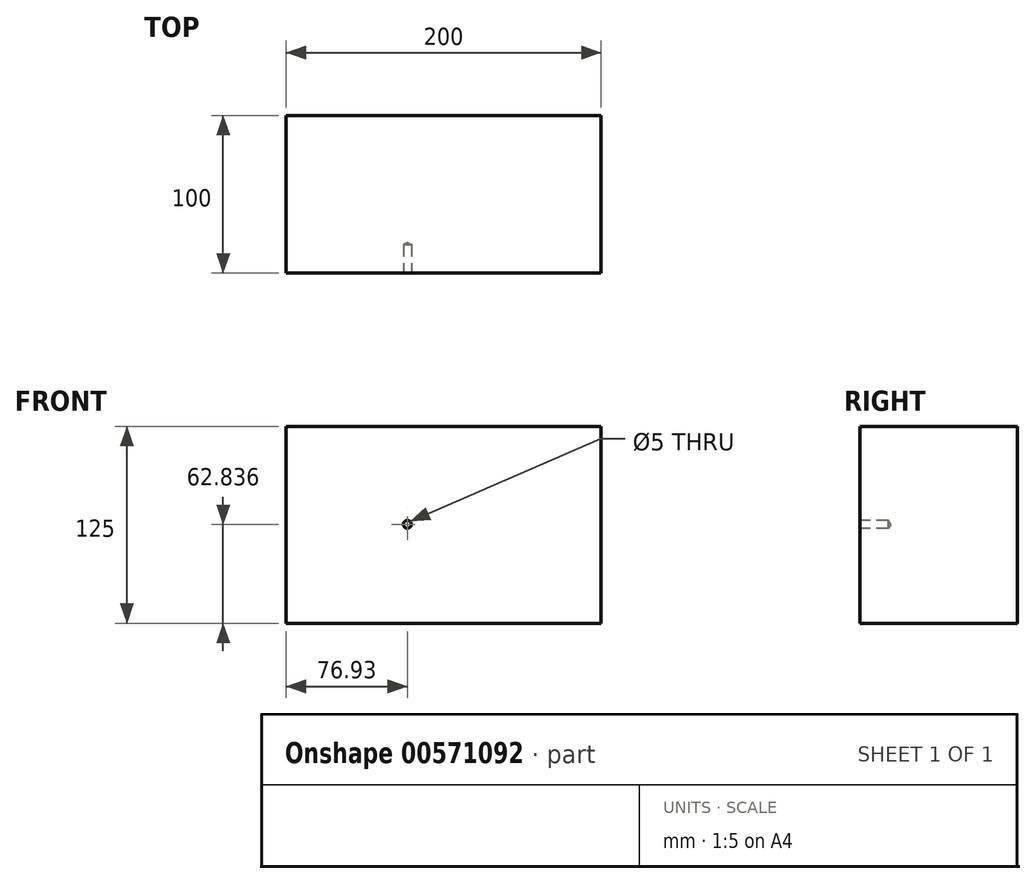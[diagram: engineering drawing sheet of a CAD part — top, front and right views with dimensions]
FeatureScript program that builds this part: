
annotation { "Feature Type Name" : "Feature", "Feature Type Description" : "" }
export const myFeature = defineFeature(function(context is Context, id is Id, definition is map)
    precondition{}
    {
        {
            var Q0;
            Q0=qCreatedBy(makeId("Front.planeOp"),FACE);
            var sketch = newSketch(context, id + "F0", { "sketchPlane" : qUnion([Q0])});
            skLineSegment(sketch, "E0.bottom", {"start": v(-100, 50) * mm, "end": v(100, 50) * mm});
            skLineSegment(sketch, "E0.top", {"start": v(-100, -50) * mm, "end": v(100, -50) * mm});
            skLineSegment(sketch, "E0.left", {"start": v(-100, 50) * mm, "end": v(-100, -50) * mm});
            skLineSegment(sketch, "E0.right", {"start": v(100, 50) * mm, "end": v(100, -50) * mm});
            skPoint(sketch, "E0.middle", {"position": v(0, 0) * mm});
            skSolve(sketch);
        }
        {
            var Q0;
            Q0 = qSketchRegion(id + "F0", true);
            extrude(context, id + "F1", {"entities" : qUnion([Q0]), "endBound" : BoundingType.SYMMETRIC, "depth" : 100 * mm, "offsetDistance" : 25 * mm});
        }
        {
            var Q0;
            Q0=makeQuery(id+"F1.opExtrude","CAP_FACE",FACE,{"disambiguationData":[OSD([sQuery(id+"F0.wireOp",EDGE,"E0.bottom"),sQuery(id+"F0.wireOp",EDGE,"E0.top"),sQuery(id+"F0.wireOp",EDGE,"E0.left"),sQuery(id+"F0.wireOp",EDGE,"E0.right")])],"isStart":false});
            var sketch = newSketch(context, id + "F2", { "sketchPlane" : qUnion([Q0])});
            skPoint(sketch, "E1", {"position": v(-23.07, 12.84) * mm});
            skSolve(sketch);
        }
        {
            var Q0;
            Q0=sQuery(id+"F2.wireOp",VERTEX,"E1");
            var Q1;
            Q1=makeQuery(id+"F1.opExtrude","SWEPT_BODY",BODY,{"disambiguationData":[OSD([sQuery(id+"F0.wireOp",EDGE,"E0.bottom"),sQuery(id+"F0.wireOp",EDGE,"E0.top"),sQuery(id+"F0.wireOp",EDGE,"E0.left"),sQuery(id+"F0.wireOp",EDGE,"E0.right")])]});
            hole(context, id + "F3", {"style" : HoleStyle.SIMPLE, "endStyle" : HoleEndStyle.BLIND, "standardTappedOrClearance" : lookupTablePath({ "standard" : "ISO", "engagement" : "75%", "pitch" : "1 mm", "size" : "M6", "type" : "Tapped" }), "standardBlindInLast" : lookupTablePath({ "standard" : "ISO", "engagement" : "75%", "pitch" : "1 mm", "size" : "M6", "type" : "Tapped" }), "holeDiameter" : 5 * mm, "showTappedDepth" : true, "holeDepth" : 18 * mm, "isTappedThrough" : true, "tappedDepth" : 15 * mm, "tapClearance" : 3, "startFromSketch" : true, "locations" : qUnion([Q0]), "scope" : qUnion([Q1]), "majorDiameter" : 6 * mm});
        }
        {
            var Q0;
            Q0=makeQuery(id+"F1.opExtrude","SWEPT_FACE",FACE,{"disambiguationData":[OSD([sQuery(id+"F0.wireOp",EDGE,"E0.bottom")])]});
            extrude(context, id + "F4", {"entities" : qUnion([Q0]), "operationType" : NewBodyOperationType.ADD, "depth" : 25 * mm, "offsetDistance" : 25 * mm});
        }
    });
